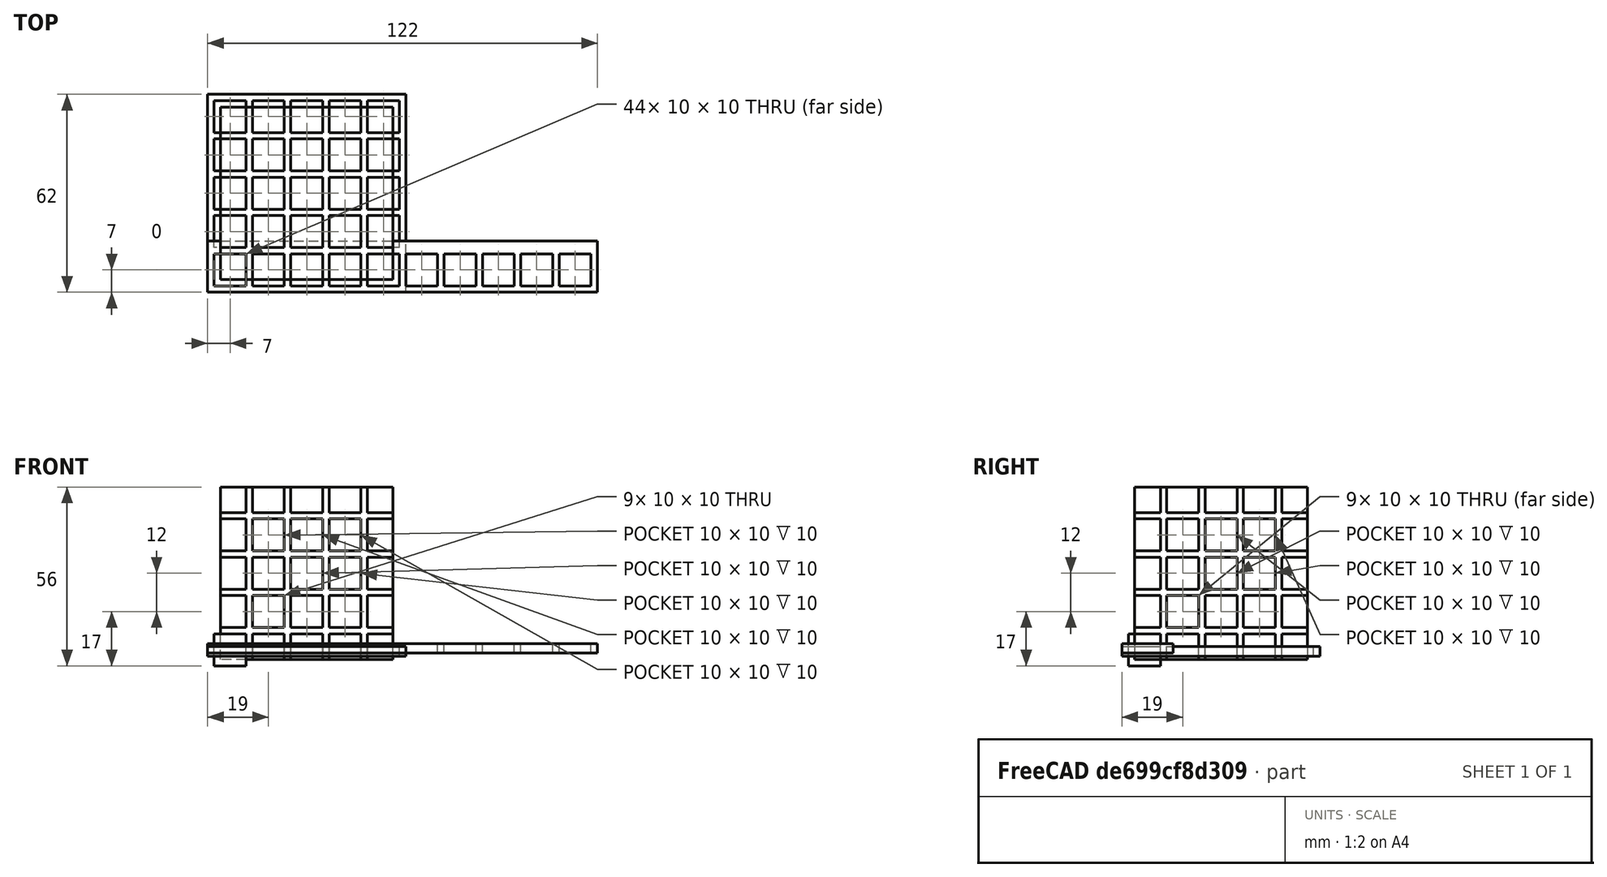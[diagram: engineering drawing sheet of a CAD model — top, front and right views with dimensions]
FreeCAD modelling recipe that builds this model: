
FCSTD DOCUMENT  (FreeCAD 0.21R33694 (Git))
Label: OJT1_T09P01_repeticion
License: All rights reserved
LicenseURL: http://en.wikipedia.org/wiki/All_rights_reserved
objects: Part::Box×6, Part::FeaturePython×3, Part::Cut×3
note: 9 computed .brp shape members not serialized (recipe doc carries the construction recipe); baked Part::Feature solids carry a one-line shape summary decoded from their .brp

FEATURE [Part::Box] Box  label="Cube"
  AttacherType = Attacher::AttachEngine3D
  Height = 10
  Length = 10
  Width = 10
FEATURE [Part::FeaturePython] Array  # Draft array (typed FeaturePython)
  AlwaysSyncPlacement = false
  Angle = 360
  ArrayType = 0
  Axis = (0,0,1)
  Base = -> Box
  Center = (0,0,0)
  Count = 10
  ExpandArray = false
  Fuse = false
  IntervalAxis = (0,0,0)
  IntervalX = (12,0,0)
  IntervalY = (0,100,0)
  IntervalZ = (0,0,100)
  NumberCircles = 3
  NumberPolar = 5
  NumberX = 10
  NumberY = 1
  NumberZ = 1
  PlacementList = 10 placements: arithmetic series from (0,0,0) step (12,0,0) to (108,0,0)
  RadialDistance = 50
  ScaleList = (10) [(1,1,1),(1,1,1),(1,1,1),(1,1,1),(1,1,1),(1,1,1),(1,1,1),(1,1,1),(1,1,1),(1,1,1)]
  Symmetry = 1
  TangentialDistance = 25
FEATURE [Part::Box] Box001  label="Cube001"
  AttacherType = Attacher::AttachEngine3D
  Height = 3
  Length = 122
  Placement = pos=(-2,-2,4) rot=(0,0,1;0rad)
  Width = 16
FEATURE [Part::Cut] Cut
  Base = -> Box001
  Refine = true
  Tool = -> Array
FEATURE [Part::Box] Box002  label="Cube002"
  AttacherType = Attacher::AttachEngine3D
  Height = 10
  Length = 10
  Width = 10
FEATURE [Part::FeaturePython] Array001  # Draft array (typed FeaturePython)
  AlwaysSyncPlacement = false
  Angle = 360
  ArrayType = 0
  Axis = (0,0,1)
  Base = -> Box002
  Center = (0,0,0)
  Count = 25
  ExpandArray = false
  Fuse = false
  IntervalAxis = (0,0,0)
  IntervalX = (12,0,0)
  IntervalY = (0,12,0)
  IntervalZ = (0,0,100)
  NumberCircles = 3
  NumberPolar = 5
  NumberX = 5
  NumberY = 5
  NumberZ = 1
  PlacementList = 25 placements: [(0,0,0),(0,12,0),(0,24,0),(0,36,0),(0,48,0),(12,0,0),(12,12,0),(12,24,0),(12,36,0),(12,48,0),(24,0,0),(24,12,0),(24,24,0),(24,36,0),(24,48,0),(36,0,0),(36,12,0),(36,24,0),(36,36,0),(36,48,0),(48,0,0),(48,12,0),(48,24,0),(48,36,0),(48,48,0)]
  RadialDistance = 50
  ScaleList = (25) [(1,1,1),(1,1,1),(1,1,1),(1,1,1),(1,1,1),(1,1,1),(1,1,1),(1,1,1),(1,1,1),(1,1,1),(1,1,1),(1,1,1),(1,1,1),(1,1,1),(1,1,1),(1,1,1),(1,1,1),(1,1,1),+7 more]
  Symmetry = 1
  TangentialDistance = 25
FEATURE [Part::Box] Box003  label="Cube003"
  AttacherType = Attacher::AttachEngine3D
  Height = 3
  Length = 62
  Placement = pos=(-2,-2,3) rot=(0,0,1;0rad)
  Width = 62
FEATURE [Part::Cut] Cut001
  Base = -> Box003
  Refine = true
  Tool = -> Array001
FEATURE [Part::Box] Box004  label="Cube004"
  AttacherType = Attacher::AttachEngine3D
  Height = 10
  Length = 10
  Width = 10
FEATURE [Part::FeaturePython] Array002  # Draft array (typed FeaturePython)
  AlwaysSyncPlacement = false
  Angle = 360
  ArrayType = 0
  Axis = (0,0,1)
  Base = -> Box004
  Center = (0,0,0)
  Count = 125
  ExpandArray = false
  Fuse = false
  IntervalAxis = (0,0,0)
  IntervalX = (12,0,0)
  IntervalY = (0,12,0)
  IntervalZ = (0,0,12)
  NumberCircles = 3
  NumberPolar = 5
  NumberX = 5
  NumberY = 5
  NumberZ = 5
  PlacementList = 125 placements: [(0,0,0),(0,0,12),(0,0,24),(0,0,36),(0,0,48),(0,12,0),(0,12,12),(0,12,24),(0,12,36),(0,12,48),(0,24,0),(0,24,12),(0,24,24),(0,24,36),(0,24,48),(0,36,0),(0,36,12),(0,36,24),(0,36,36),(0,36,48),(0,48,0),(0,48,12),(0,48,24),(0,48,36),(0,48,48),(12,0,0),(12,0,12),(12,0,24),(12,0,36),(12,0,48),(12,12,0),(12,12,12),(12,12,24),(12,12,36),(12,12,48),(12,24,0),(12,24,12),(12,24,24),(12,24,36),(12,24,48),+85 more]
  RadialDistance = 50
  ScaleList = (125) [(1,1,1),(1,1,1),(1,1,1),(1,1,1),(1,1,1),(1,1,1),(1,1,1),(1,1,1),(1,1,1),(1,1,1),(1,1,1),(1,1,1),(1,1,1),(1,1,1),(1,1,1),(1,1,1),(1,1,1),(1,1,1),+107 more]
  Symmetry = 1
  TangentialDistance = 25
FEATURE [Part::Box] Box005  label="Cube005"
  AttacherType = Attacher::AttachEngine3D
  Height = 54
  Length = 54
  Placement = pos=(2,2,2) rot=(0,0,1;0rad)
  Width = 54
FEATURE [Part::Cut] Cut002
  Base = -> Box005
  Refine = true
  Tool = -> Array002
